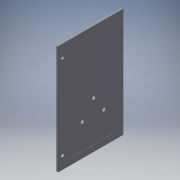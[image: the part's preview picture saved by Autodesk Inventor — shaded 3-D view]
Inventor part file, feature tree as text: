
AUTODESK INVENTOR PART (.ipt)
format: ipt  version: 2017 (Build 210142000, 142)  size: 801,792 bytes
history: native  units: in
note: dims shown in document units (in); Inventor stores cm internally (conversion verified against a paired STEP export)
features: hole x3, other x1
ambient origin geometry x8: Origin, YZ Plane, XZ Plane, XY Plane, X Axis, Y Axis, Z Axis, Center Point
bodies: Solid1 (feature_tree)
feature tree (4):
  other  "nsycrn106250t"
  hole  "Hole1"  [1 undecoded]
  hole  "Hole2"  [1 undecoded]
  hole  "Hole3"  [1 undecoded]
note: 3 required parameter values undecoded (feature->parameter linkage not recoverable at this tier; creation-order binding heuristic only, values carry confidence <= 0.55)
